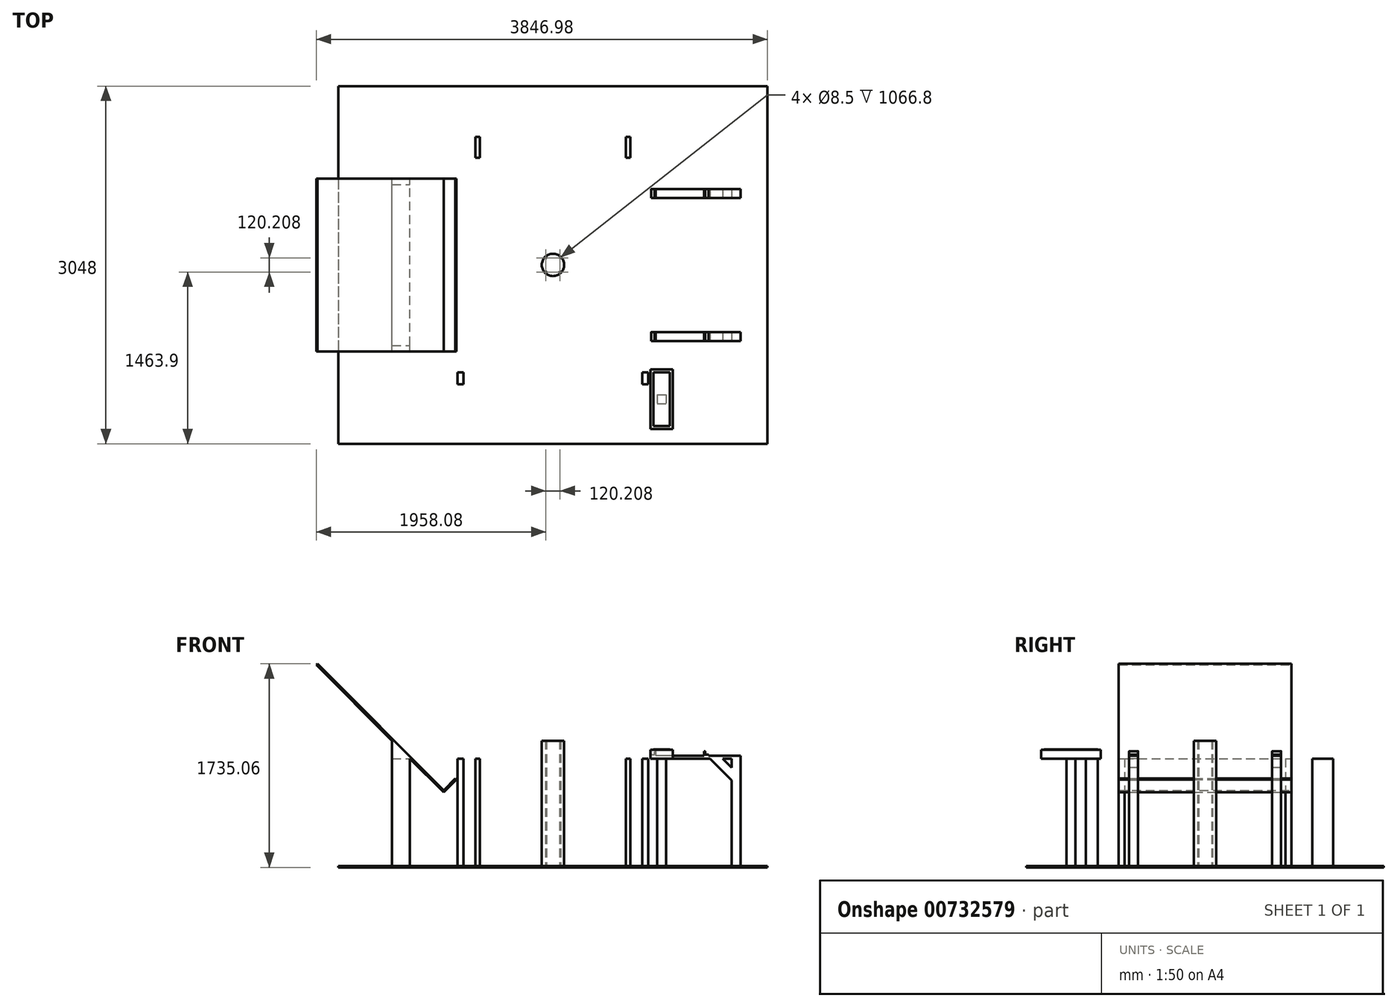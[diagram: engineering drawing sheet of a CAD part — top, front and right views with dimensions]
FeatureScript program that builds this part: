
annotation { "Feature Type Name" : "Feature", "Feature Type Description" : "" }
export const myFeature = defineFeature(function(context is Context, id is Id, definition is map)
    precondition{}
    {
        {
            var Q0;
            Q0=qCreatedBy(makeId("Top.planeOp"),FACE);
            var sketch = newSketch(context, id + "F0", { "sketchPlane" : qUnion([Q0])});
            skLineSegment(sketch, "E0.bottom", {"start": v(1828.8, 1524) * mm, "end": v(-1828.8, 1524) * mm});
            skLineSegment(sketch, "E0.top", {"start": v(1828.8, -1524) * mm, "end": v(-1828.8, -1524) * mm});
            skLineSegment(sketch, "E0.left", {"start": v(1828.8, 1524) * mm, "end": v(1828.8, -1524) * mm});
            skLineSegment(sketch, "E0.right", {"start": v(-1828.8, 1524) * mm, "end": v(-1828.8, -1524) * mm});
            skPoint(sketch, "E0.middle", {"position": v(0, 0) * mm});
            skSolve(sketch);
        }
        {
            var Q0;
            Q0 = qSketchRegion(id + "F0", true);
            extrude(context, id + "F1", {"entities" : qUnion([Q0]), "depth" : 12.7 * mm, "offsetDistance" : 25.4 * mm});
        }
        {
            var Q0;
            Q0=makeQuery(id+"F1.opExtrude","CAP_FACE",FACE,{"disambiguationData":[OSD([sQuery(id+"F0.wireOp",EDGE,"E0.bottom"),sQuery(id+"F0.wireOp",EDGE,"E0.top"),sQuery(id+"F0.wireOp",EDGE,"E0.left"),sQuery(id+"F0.wireOp",EDGE,"E0.right")])],"isStart":false});
            var sketch = newSketch(context, id + "F2", { "sketchPlane" : qUnion([Q0])});
            skCircle(sketch, "E1", {"center": v(0, 0) * mm, "radius": 95.25 * mm});
            skCircle(sketch, "E2", {"center": v(0, 0) * mm, "radius": 85 * mm, "construction": true});
            skCircle(sketch, "E3", {"center": v(60.1, 60.1) * mm, "radius": 4.25 * mm});
            skCircle(sketch, "E4", {"center": v(60.1, -60.1) * mm, "radius": 4.25 * mm});
            skCircle(sketch, "E5", {"center": v(-60.1, 60.1) * mm, "radius": 4.25 * mm});
            skCircle(sketch, "E6", {"center": v(-60.1, -60.1) * mm, "radius": 4.25 * mm});
            skLineSegment(sketch, "E7", {"start": v(60.1, 60.1) * mm, "end": v(-60.1, -60.1) * mm, "construction": true});
            skLineSegment(sketch, "E8", {"start": v(-60.1, 60.1) * mm, "end": v(60.1, -60.1) * mm, "construction": true});
            skSolve(sketch);
        }
        {
            var Q0;
            Q0 = qSketchRegion(id + "F2", true);
            extrude(context, id + "F3", {"entities" : qUnion([Q0]), "operationType" : NewBodyOperationType.ADD, "depth" : 1066.8 * mm, "offsetDistance" : 25.4 * mm});
        }
        {
            var Q0;
            {var subQ0=sQuery(id+"F0.wireOp",EDGE,"E0.left");var subQ1=sQuery(id+"F0.wireOp",EDGE,"E0.top");var subQ2=sQuery(id+"F0.wireOp",EDGE,"E0.right");var subQ3=sQuery(id+"F0.wireOp",EDGE,"E0.bottom");Q0=makeQuery(id+"F3.boolean.opBoolean","SPLIT",FACE,{"disambiguationData":[TD([makeQuery(id+"F1.opExtrude","SWEPT_FACE",FACE,{"disambiguationData":[OSD([subQ3])]})])],"derivedFrom":makeQuery(id+"F1.opExtrude","CAP_FACE",FACE,{"disambiguationData":[OSD([subQ3,subQ1,subQ0,subQ2])],"isStart":false})});}
            var sketch = newSketch(context, id + "F4", { "sketchPlane" : qUnion([Q0])});
            skLineSegment(sketch, "E9.bottom", {"start": v(-622.3, 1092.2) * mm, "end": v(-660.4, 1092.2) * mm});
            skLineSegment(sketch, "E9.top", {"start": v(-622.3, 914.4) * mm, "end": v(-660.4, 914.4) * mm});
            skLineSegment(sketch, "E9.left", {"start": v(-622.3, 1092.2) * mm, "end": v(-622.3, 914.4) * mm});
            skLineSegment(sketch, "E9.right", {"start": v(-660.4, 1092.2) * mm, "end": v(-660.4, 914.4) * mm});
            skPoint(sketch, "E9.middle", {"position": v(-641.35, 1003.3) * mm});
            skLineSegment(sketch, "E10.bottom", {"start": v(660.4, 1092.2) * mm, "end": v(622.3, 1092.2) * mm});
            skLineSegment(sketch, "E10.top", {"start": v(660.4, 914.4) * mm, "end": v(622.3, 914.4) * mm});
            skLineSegment(sketch, "E10.left", {"start": v(660.4, 1092.2) * mm, "end": v(660.4, 914.4) * mm});
            skLineSegment(sketch, "E10.right", {"start": v(622.3, 1092.2) * mm, "end": v(622.3, 914.4) * mm});
            skPoint(sketch, "E10.middle", {"position": v(641.35, 1003.3) * mm});
            skLineSegment(sketch, "E11.bottom", {"start": v(-812.8, -1016) * mm, "end": v(-762, -1016) * mm});
            skLineSegment(sketch, "E11.top", {"start": v(-812.8, -914.4) * mm, "end": v(-762, -914.4) * mm});
            skLineSegment(sketch, "E11.left", {"start": v(-812.8, -1016) * mm, "end": v(-812.8, -914.4) * mm});
            skLineSegment(sketch, "E11.right", {"start": v(-762, -1016) * mm, "end": v(-762, -914.4) * mm});
            skLineSegment(sketch, "E12.bottom", {"start": v(762, -914.4) * mm, "end": v(812.8, -914.4) * mm});
            skLineSegment(sketch, "E12.top", {"start": v(762, -1016) * mm, "end": v(812.8, -1016) * mm});
            skLineSegment(sketch, "E12.left", {"start": v(762, -914.4) * mm, "end": v(762, -1016) * mm});
            skLineSegment(sketch, "E12.right", {"start": v(812.8, -914.4) * mm, "end": v(812.8, -1016) * mm});
            skLineSegment(sketch, "E13.bottom", {"start": v(1524, 571.5) * mm, "end": v(1600.2, 571.5) * mm});
            skLineSegment(sketch, "E13.top", {"start": v(1524, 647.7) * mm, "end": v(1600.2, 647.7) * mm});
            skLineSegment(sketch, "E13.left", {"start": v(1524, 571.5) * mm, "end": v(1524, 647.7) * mm});
            skLineSegment(sketch, "E13.right", {"start": v(1600.2, 571.5) * mm, "end": v(1600.2, 647.7) * mm});
            skLineSegment(sketch, "E14.bottom", {"start": v(1524, -571.5) * mm, "end": v(1600.2, -571.5) * mm});
            skLineSegment(sketch, "E14.top", {"start": v(1524, -647.7) * mm, "end": v(1600.2, -647.7) * mm});
            skLineSegment(sketch, "E14.left", {"start": v(1524, -571.5) * mm, "end": v(1524, -647.7) * mm});
            skLineSegment(sketch, "E14.right", {"start": v(1600.2, -571.5) * mm, "end": v(1600.2, -647.7) * mm});
            skLineSegment(sketch, "E15.bottom", {"start": v(889, -1104.9) * mm, "end": v(965.2, -1104.9) * mm});
            skLineSegment(sketch, "E15.top", {"start": v(889, -1181.1) * mm, "end": v(965.2, -1181.1) * mm});
            skLineSegment(sketch, "E15.left", {"start": v(889, -1104.9) * mm, "end": v(889, -1181.1) * mm});
            skLineSegment(sketch, "E15.right", {"start": v(965.2, -1104.9) * mm, "end": v(965.2, -1181.1) * mm});
            skSolve(sketch);
        }
        {
            var Q0;
            Q0 = qSketchRegion(id + "F4", true);
            extrude(context, id + "F5", {"entities" : qUnion([Q0]), "operationType" : NewBodyOperationType.ADD, "depth" : 914.4 * mm, "offsetDistance" : 25.4 * mm});
        }
        {
            var Q0;
            {var subQ0=sQuery(id+"F0.wireOp",EDGE,"E0.left");var subQ1=sQuery(id+"F0.wireOp",EDGE,"E0.top");var subQ2=sQuery(id+"F0.wireOp",EDGE,"E0.right");var subQ3=sQuery(id+"F0.wireOp",EDGE,"E0.bottom");Q0=makeQuery(id+"F3.boolean.opBoolean","SPLIT",FACE,{"disambiguationData":[TD([makeQuery(id+"F1.opExtrude","SWEPT_FACE",FACE,{"disambiguationData":[OSD([subQ3])]})])],"derivedFrom":makeQuery(id+"F1.opExtrude","CAP_FACE",FACE,{"disambiguationData":[OSD([subQ3,subQ1,subQ0,subQ2])],"isStart":false})});}
            var sketch = newSketch(context, id + "F6", { "sketchPlane" : qUnion([Q0])});
            skLineSegment(sketch, "E16.bottom", {"start": v(-1371.6, 685.8) * mm, "end": v(-1219.2, 685.8) * mm});
            skLineSegment(sketch, "E16.top", {"start": v(-1371.6, 736.6) * mm, "end": v(-1219.2, 736.6) * mm});
            skLineSegment(sketch, "E16.left", {"start": v(-1371.6, 685.8) * mm, "end": v(-1371.6, 736.6) * mm});
            skLineSegment(sketch, "E16.right", {"start": v(-1219.2, 685.8) * mm, "end": v(-1219.2, 736.6) * mm});
            skLineSegment(sketch, "E17.bottom", {"start": v(-1371.6, -736.6) * mm, "end": v(-1219.2, -736.6) * mm});
            skLineSegment(sketch, "E17.top", {"start": v(-1371.6, -685.8) * mm, "end": v(-1219.2, -685.8) * mm});
            skLineSegment(sketch, "E17.left", {"start": v(-1371.6, -736.6) * mm, "end": v(-1371.6, -685.8) * mm});
            skLineSegment(sketch, "E17.right", {"start": v(-1219.2, -736.6) * mm, "end": v(-1219.2, -685.8) * mm});
            skSolve(sketch);
        }
        {
            var Q0;
            Q0 = qSketchRegion(id + "F6", true);
            extrude(context, id + "F7", {"entities" : qUnion([Q0]), "operationType" : NewBodyOperationType.ADD, "depth" : 914.4 * mm, "offsetDistance" : 25.4 * mm});
        }
        {
            var Q0;
            Q0=qCreatedBy(makeId("Front.planeOp"),FACE);
            var sketch = newSketch(context, id + "F8", { "sketchPlane" : qUnion([Q0])});
            skLineSegment(sketch, "E18", {"start": v(-1371.6, 927.1) * mm, "end": v(-1371.6, 1079.5) * mm});
            skLineSegment(sketch, "E19", {"start": v(-1371.6, 1079.5) * mm, "end": v(-2018.18, 1726.08) * mm});
            skLineSegment(sketch, "E20", {"start": v(-2018.18, 1726.08) * mm, "end": v(-2009.2, 1735.06) * mm});
            skLineSegment(sketch, "E21", {"start": v(-2009.2, 1735.06) * mm, "end": v(-931.57, 657.43) * mm});
            skLineSegment(sketch, "E22", {"start": v(-931.57, 657.43) * mm, "end": v(-832.78, 756.21) * mm});
            skLineSegment(sketch, "E23", {"start": v(-832.78, 756.21) * mm, "end": v(-823.8, 747.23) * mm});
            skLineSegment(sketch, "E24", {"start": v(-823.8, 747.23) * mm, "end": v(-931.57, 639.47) * mm});
            skLineSegment(sketch, "E25", {"start": v(-931.57, 639.47) * mm, "end": v(-1219.2, 927.1) * mm});
            skLineSegment(sketch, "E26", {"start": v(-1219.2, 927.1) * mm, "end": v(-1371.6, 927.1) * mm});
            skSolve(sketch);
        }
        {
            var Q0;
            Q0 = qSketchRegion(id + "F8", true);
            var Q1;
            Q1=makeQuery(id+"F7.opExtrude","SWEPT_FACE",FACE,{"disambiguationData":[OSD([sQuery(id+"F6.wireOp",EDGE,"E17.bottom")])]});
            var Q2;
            Q2=makeQuery(id+"F7.opExtrude","SWEPT_FACE",FACE,{"disambiguationData":[OSD([sQuery(id+"F6.wireOp",EDGE,"E16.top")])]});
            extrude(context, id + "F9", {"entities" : qUnion([Q0]), "operationType" : NewBodyOperationType.ADD, "endBound" : BoundingType.UP_TO_SURFACE, "depth" : 25.4 * mm, "endBoundEntityFace" : qUnion([Q1]), "offsetDistance" : 25.4 * mm, "hasSecondDirection" : true, "secondDirectionBound" : SecondDirectionBoundingType.UP_TO_SURFACE, "secondDirectionOppositeDirection" : true, "secondDirectionDepth" : 25.4 * mm, "secondDirectionBoundEntityFace" : qUnion([Q2])});
        }
        {
            var Q0;
            Q0=makeQuery(id+"F5.opExtrude","SWEPT_FACE",FACE,{"disambiguationData":[OSD([sQuery(id+"F4.wireOp",EDGE,"E14.top")])]});
            var sketch = newSketch(context, id + "F10", { "sketchPlane" : qUnion([Q0])});
            skLineSegment(sketch, "E27.bottom", {"start": v(1600.2, 927.1) * mm, "end": v(1447.8, 927.1) * mm});
            skLineSegment(sketch, "E27.top", {"start": v(1600.2, 952.5) * mm, "end": v(1327.15, 952.5) * mm});
            skLineSegment(sketch, "E27.left", {"start": v(1600.2, 927.1) * mm, "end": v(1600.2, 952.5) * mm});
            skLineSegment(sketch, "E27.right", {"start": v(838.2, 927.1) * mm, "end": v(838.2, 962.02) * mm});
            skLineSegment(sketch, "E28", {"start": v(1340.04, 927.1) * mm, "end": v(1524, 743.14) * mm});
            skLineSegment(sketch, "E29", {"start": v(1447.8, 927.1) * mm, "end": v(1524, 850.9) * mm});
            skLineSegment(sketch, "E30", {"start": v(1524, 850.9) * mm, "end": v(1524, 743.14) * mm});
            skLineSegment(sketch, "E31.trimOffspring", {"start": v(1340.04, 927.1) * mm, "end": v(838.2, 927.1) * mm});
            skLineSegment(sketch, "E32", {"start": v(838.2, 962.02) * mm, "end": v(866.78, 962.02) * mm});
            skLineSegment(sketch, "E33", {"start": v(866.78, 962.02) * mm, "end": v(866.78, 990.6) * mm});
            skLineSegment(sketch, "E34", {"start": v(866.78, 990.6) * mm, "end": v(876.3, 990.6) * mm});
            skLineSegment(sketch, "E35", {"start": v(876.3, 990.6) * mm, "end": v(876.3, 952.5) * mm});
            skLineSegment(sketch, "E36", {"start": v(1289.05, 952.5) * mm, "end": v(1289.05, 990.6) * mm});
            skLineSegment(sketch, "E37", {"start": v(1289.05, 990.6) * mm, "end": v(1298.58, 990.6) * mm});
            skLineSegment(sketch, "E38", {"start": v(1298.58, 990.6) * mm, "end": v(1298.58, 962.03) * mm});
            skLineSegment(sketch, "E39", {"start": v(1298.58, 962.03) * mm, "end": v(1327.15, 962.03) * mm});
            skLineSegment(sketch, "E40", {"start": v(1327.15, 962.02) * mm, "end": v(1327.15, 952.5) * mm});
            skLineSegment(sketch, "E41.trimOffspring", {"start": v(1289.05, 952.5) * mm, "end": v(876.3, 952.5) * mm});
            skSolve(sketch);
        }
        {
            var Q0;
            Q0 = qSketchRegion(id + "F10", true);
            var Q1;
            Q1=makeQuery(id+"F5.opExtrude","SWEPT_FACE",FACE,{"disambiguationData":[OSD([sQuery(id+"F4.wireOp",EDGE,"E14.bottom")])]});
            extrude(context, id + "F11", {"entities" : qUnion([Q0]), "operationType" : NewBodyOperationType.ADD, "endBound" : BoundingType.UP_TO_SURFACE, "oppositeDirection" : true, "depth" : 25.4 * mm, "endBoundEntityFace" : qUnion([Q1]), "offsetDistance" : 25.4 * mm});
        }
        {
            var Q0;
            Q0=makeQuery(id+"F5.opExtrude","SWEPT_FACE",FACE,{"disambiguationData":[OSD([sQuery(id+"F4.wireOp",EDGE,"E13.bottom")])]});
            var sketch = newSketch(context, id + "F12", { "sketchPlane" : qUnion([Q0])});
            skLineSegment(sketch, "E42.bottom", {"start": v(1600.2, 927.1) * mm, "end": v(1447.8, 927.1) * mm});
            skLineSegment(sketch, "E42.top", {"start": v(1600.2, 952.5) * mm, "end": v(1327.15, 952.5) * mm});
            skLineSegment(sketch, "E42.left", {"start": v(1600.2, 927.1) * mm, "end": v(1600.2, 952.5) * mm});
            skLineSegment(sketch, "E42.right", {"start": v(838.2, 927.1) * mm, "end": v(838.2, 962.02) * mm});
            skLineSegment(sketch, "E43", {"start": v(1340.04, 927.1) * mm, "end": v(1600.2, 666.94) * mm});
            skLineSegment(sketch, "E44", {"start": v(1447.8, 927.1) * mm, "end": v(1600.2, 774.7) * mm});
            skLineSegment(sketch, "E45", {"start": v(1600.2, 774.7) * mm, "end": v(1600.2, 666.94) * mm});
            skLineSegment(sketch, "E46.trimOffspring", {"start": v(1340.04, 927.1) * mm, "end": v(838.2, 927.1) * mm});
            skLineSegment(sketch, "E47", {"start": v(838.2, 962.02) * mm, "end": v(866.78, 962.02) * mm});
            skLineSegment(sketch, "E48", {"start": v(866.78, 962.03) * mm, "end": v(866.78, 990.6) * mm});
            skLineSegment(sketch, "E49", {"start": v(866.78, 990.6) * mm, "end": v(876.3, 990.6) * mm});
            skLineSegment(sketch, "E50", {"start": v(876.3, 990.6) * mm, "end": v(876.3, 952.5) * mm});
            skLineSegment(sketch, "E51", {"start": v(1289.05, 952.5) * mm, "end": v(1289.05, 990.6) * mm});
            skLineSegment(sketch, "E52", {"start": v(1289.05, 990.6) * mm, "end": v(1298.58, 990.6) * mm});
            skLineSegment(sketch, "E53", {"start": v(1298.58, 990.6) * mm, "end": v(1298.58, 962.03) * mm});
            skLineSegment(sketch, "E54", {"start": v(1298.58, 962.03) * mm, "end": v(1327.15, 962.03) * mm});
            skLineSegment(sketch, "E55", {"start": v(1327.15, 962.03) * mm, "end": v(1327.15, 952.5) * mm});
            skLineSegment(sketch, "E56.trimOffspring", {"start": v(1289.05, 952.5) * mm, "end": v(876.3, 952.5) * mm});
            skSolve(sketch);
        }
        {
            var Q0;
            Q0 = qSketchRegion(id + "F12", true);
            var Q1;
            Q1=makeQuery(id+"F5.opExtrude","SWEPT_FACE",FACE,{"disambiguationData":[OSD([sQuery(id+"F4.wireOp",EDGE,"E13.top")])]});
            extrude(context, id + "F13", {"entities" : qUnion([Q0]), "operationType" : NewBodyOperationType.ADD, "endBound" : BoundingType.UP_TO_SURFACE, "oppositeDirection" : true, "depth" : 25.4 * mm, "endBoundEntityFace" : qUnion([Q1]), "offsetDistance" : 25.4 * mm});
        }
        {
            var Q0;
            Q0=makeQuery(id+"F11.opExtrude","SWEPT_EDGE",EDGE,{"disambiguationData":[OSD([sQuery(id+"F10.wireOp",EDGE,"E33"),sQuery(id+"F10.wireOp",EDGE,"E34")])]});
            var Q1;
            Q1=makeQuery(id+"F11.opExtrude","SWEPT_EDGE",EDGE,{"disambiguationData":[OSD([sQuery(id+"F10.wireOp",EDGE,"VWNxP4j7-PjH9-B9Y1-3Q6L-4AkbbHdYOtBc"),sQuery(id+"F10.wireOp",EDGE,"E32")])]});
            var Q2;
            Q2=makeQuery(id+"F11.opExtrude","SWEPT_EDGE",EDGE,{"disambiguationData":[OSD([sQuery(id+"F10.wireOp",EDGE,"E37"),sQuery(id+"F10.wireOp",EDGE,"E38")])]});
            var Q3;
            Q3=makeQuery(id+"F11.opExtrude","SWEPT_EDGE",EDGE,{"disambiguationData":[OSD([sQuery(id+"F10.wireOp",EDGE,"E39"),sQuery(id+"F10.wireOp",EDGE,"E40")])]});
            var Q4;
            Q4=makeQuery(id+"F13.opExtrude","SWEPT_EDGE",EDGE,{"disambiguationData":[OSD([sQuery(id+"F12.wireOp",EDGE,"E48"),sQuery(id+"F12.wireOp",EDGE,"E49")])]});
            var Q5;
            Q5=makeQuery(id+"F13.opExtrude","SWEPT_EDGE",EDGE,{"disambiguationData":[OSD([sQuery(id+"F12.wireOp",EDGE,"E42.right"),sQuery(id+"F12.wireOp",EDGE,"E47")])]});
            var Q6;
            Q6=makeQuery(id+"F13.opExtrude","SWEPT_EDGE",EDGE,{"disambiguationData":[OSD([sQuery(id+"F12.wireOp",EDGE,"E52"),sQuery(id+"F12.wireOp",EDGE,"E53")])]});
            var Q7;
            Q7=makeQuery(id+"F13.opExtrude","SWEPT_EDGE",EDGE,{"disambiguationData":[OSD([sQuery(id+"F12.wireOp",EDGE,"E54"),sQuery(id+"F12.wireOp",EDGE,"E55")])]});
            fillet(context, id + "F14", {"entities" : qUnion([Q0, Q1, Q2, Q3, Q4, Q5, Q6, Q7]), "radius" : 6.35 * mm, "tangentPropagation" : true, "allowEdgeOverflow" : false});
        }
        {
            var Q0;
            Q0=makeQuery(id+"F5.opExtrude","CAP_FACE",FACE,{"disambiguationData":[OSD([sQuery(id+"F4.wireOp",EDGE,"E15.bottom"),sQuery(id+"F4.wireOp",EDGE,"E15.top"),sQuery(id+"F4.wireOp",EDGE,"E15.left"),sQuery(id+"F4.wireOp",EDGE,"E15.right")])],"isStart":false});
            var sketch = newSketch(context, id + "F15", { "sketchPlane" : qUnion([Q0])});
            skLineSegment(sketch, "E57.bottom", {"start": v(1022.35, -889) * mm, "end": v(831.85, -889) * mm});
            skLineSegment(sketch, "E57.top", {"start": v(1022.35, -1397) * mm, "end": v(831.85, -1397) * mm});
            skLineSegment(sketch, "E57.left", {"start": v(1022.35, -889) * mm, "end": v(1022.35, -1397) * mm});
            skLineSegment(sketch, "E57.right", {"start": v(831.85, -889) * mm, "end": v(831.85, -1397) * mm});
            skPoint(sketch, "E57.middle", {"position": v(927.1, -1143) * mm});
            skSolve(sketch);
        }
        {
            var Q0;
            Q0 = qSketchRegion(id + "F15", true);
            extrude(context, id + "F16", {"entities" : qUnion([Q0]), "operationType" : NewBodyOperationType.ADD, "depth" : 76.2 * mm, "offsetDistance" : 25.4 * mm});
        }
        {
            var Q0;
            Q0=makeQuery(id+"F16.opExtrude","CAP_FACE",FACE,{"disambiguationData":[OSD([sQuery(id+"F15.wireOp",EDGE,"E57.bottom"),sQuery(id+"F15.wireOp",EDGE,"E57.top"),sQuery(id+"F15.wireOp",EDGE,"E57.left"),sQuery(id+"F15.wireOp",EDGE,"E57.right")])],"isStart":false});
            var sketch = newSketch(context, id + "F17", { "sketchPlane" : qUnion([Q0])});
            skLineSegment(sketch, "E58.bottom", {"start": v(996.95, -1371.6) * mm, "end": v(857.25, -1371.6) * mm});
            skLineSegment(sketch, "E58.top", {"start": v(996.95, -914.4) * mm, "end": v(857.25, -914.4) * mm});
            skLineSegment(sketch, "E58.left", {"start": v(996.95, -1371.6) * mm, "end": v(996.95, -914.4) * mm});
            skLineSegment(sketch, "E58.right", {"start": v(857.25, -1371.6) * mm, "end": v(857.25, -914.4) * mm});
            skPoint(sketch, "E58.middle", {"position": v(927.1, -1143) * mm});
            skPoint(sketch, "E58.middle.positionSnap0", {"position": v(927.1, -889) * mm});
            skPoint(sketch, "E58.middle.positionSnap1", {"position": v(1022.35, -1143) * mm});
            skPoint(sketch, "E58.centerSnap0", {"position": v(927.1, -889) * mm});
            skPoint(sketch, "E58.centerSnap1", {"position": v(1022.35, -1143) * mm});
            skSolve(sketch);
        }
        {
            var Q0;
            Q0 = qSketchRegion(id + "F17", true);
            extrude(context, id + "F18", {"entities" : qUnion([Q0]), "depth" : 0.64 * mm, "offsetDistance" : 25.4 * mm});
        }
    });
